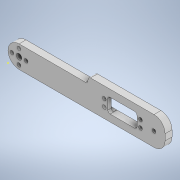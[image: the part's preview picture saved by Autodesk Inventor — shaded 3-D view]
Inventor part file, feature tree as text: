
AUTODESK INVENTOR PART (.ipt)
format: ipt  version: 2020.1 (Build 241239000, 239)  size: 319,488 bytes
history: native  units: in
note: dims shown in document units (in); Inventor stores cm internally (conversion verified against a paired STEP export)
features: sketch x16, extrude x10, fillet x6
ambient origin geometry x8: Origin, YZ Plane, XZ Plane, XY Plane, X Axis, Y Axis, Z Axis, Center Point
bodies: Solid1 (feature_tree)
feature tree (32):
  sketch  "Sketch1"  dims[d0=8.5in d1=2.0in]
  extrude  "Extrusion1"  Depth=8.5in
  extrude  "Extrusion2"  Depth=1.2in
  extrude  "Extrusion3"  Depth=1.2in
  extrude  "Extrusion4"  Depth=1.0in
  extrude  "Extrusion5"  Depth=0.375in
  extrude  "Extrusion6"  Depth=1.5827in
  sketch  "Sketch8"  dims[d20=0.173in d21=0.1772in]
  sketch  "Sketch9"  dims[d22=0.3898in d23=0.177in d24=0.189in d25=0.173in d26=0.177in]
  sketch  "Sketch10"  dims[d27=0.39in d28=0.177in]
  fillet  "Fillet1"  Radius=0.7874in
  fillet  "Fillet2"  Radius=1.0in
  fillet  "Fillet3"  Radius=1.2in
  extrude  "Extrusion7"  Depth=0.189in
  extrude  "Extrusion8"  Depth=0.1772in
  sketch  "Sketch13"  dims[d33=0.177in]
  sketch  "Sketch14"  dims[d34=1.0in d35=0.0in]
  extrude  "Extrusion9"  Depth=0.177in
  fillet  "Fillet4"  Radius=0.189in
  fillet  "Fillet5"  Radius=0.173in
  fillet  "Fillet6"  Radius=0.177in
  extrude  "Extrusion10"  Depth=0.177in
  sketch  "Sketch2"  dims[d2=0.375in d3=0.0in d4=1.2in]
  sketch  "Sketch3"  dims[d5=1.2in d6=0.5in]
  sketch  "Sketch4"  dims[d7=1.0in d8=1.0in]
  sketch  "Sketch5"  dims[d9=1.6in d10=0.375in]
  sketch  "Sketch6"  dims[d11=1.6in d12=1.5827in d13=0.7874in d14=1.0in d15=0.0in d16=1.2in]
  sketch  "Sketch7"  dims[d17=1.0in d18=0.0in d19=0.189in]
  sketch  "Sketch11"  dims[d29=1.0in d30=0.0in]
  sketch  "Sketch12"  dims[d31=0.1875in d32=0.0in]
  sketch  "Sketch15"  dims[d36=0.125in]
  sketch  "Sketch16"  dims[d37=0.125in d38=0.6in d39=0.6in d40=0.3in d41=0.107in d42=0.107in d43=0.107in d44=0.107in d45=1.0in d46=0.0in d47=0.177in d48=0.177in d49=0.177in d50=0.177in d51=0.2in d52=0.2in d53=0.2in d54=0.2in d55=0.2in d56=0.2in d57=0.2in d58=0.2in d59=0.2in d60=1.0in d61=0.0in d62=0.375in d63=1.0in d64=0.0in d65=0.6in d66=0.125in d67=0.125in d68=0.2in d69=1.0in d70=0.0in]
